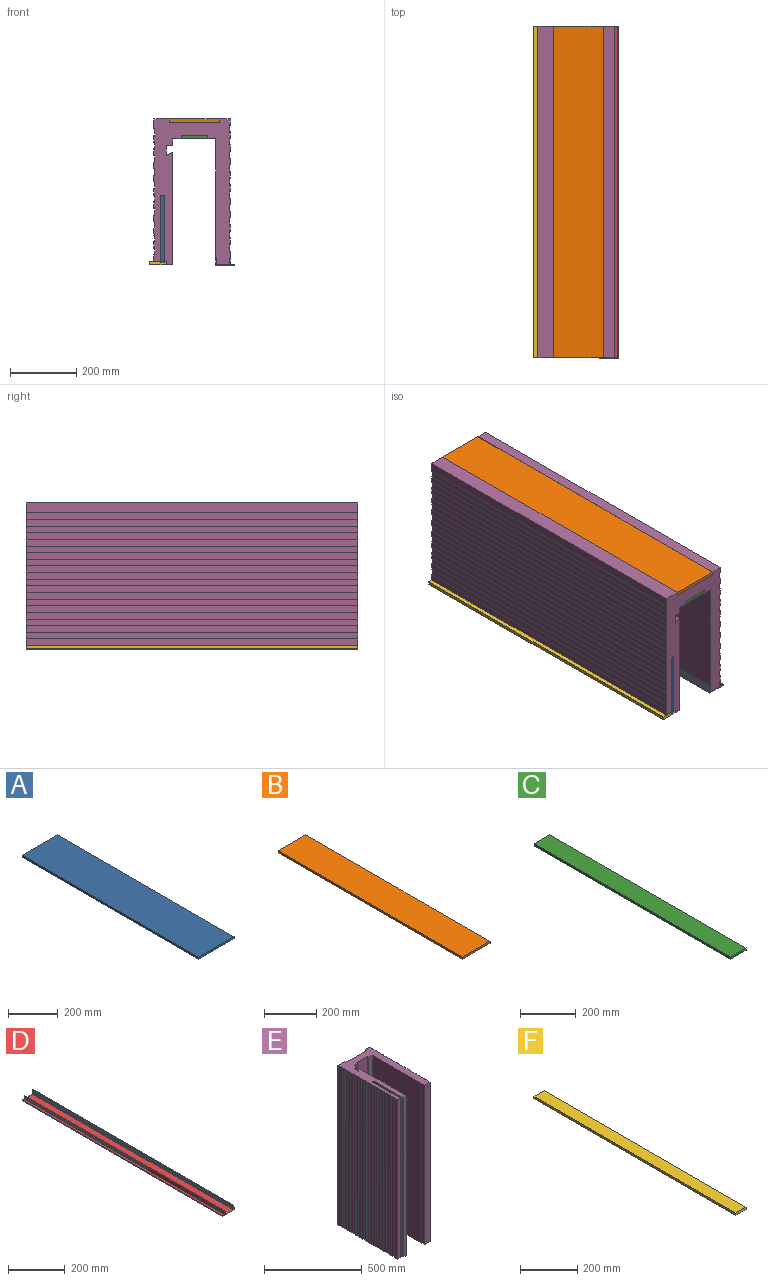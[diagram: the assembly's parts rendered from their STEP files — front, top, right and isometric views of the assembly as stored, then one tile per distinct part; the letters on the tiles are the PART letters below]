
ASSEMBLY  parts=6 mates=5
PART A: 6 faces, bbox 200x1000x10 mm
  f0: plane 1000x10mm, normal (-1,0,0), area 10000mm2, adj f1,f3,f4,f5
  f1: plane 1000x200mm, normal (0,0,-1), area 200000mm2, adj f0,f2,f4,f5
  f2: plane 1000x10mm, normal (1,0,0), area 10000mm2, adj f1,f3,f4,f5
  f3: plane 1000x200mm, normal (0,0,1), area 200000mm2, adj f0,f2,f4,f5
  f4: plane 200x10mm, normal (0,-1,0), area 2000mm2, adj f0,f1,f2,f3
  f5: plane 200x10mm, normal (0,1,0), area 2000mm2, adj f0,f1,f2,f3
PART B: 6 faces, bbox 150x1000x10 mm
  f0: plane 1000x10mm, normal (-1,0,0), area 10000mm2, adj f1,f3,f4,f5
  f1: plane 1000x150mm, normal (0,0,-1), area 150000mm2, adj f0,f2,f4,f5
  f2: plane 1000x10mm, normal (1,0,0), area 10000mm2, adj f1,f3,f4,f5
  f3: plane 1000x150mm, normal (0,0,1), area 150000mm2, adj f0,f2,f4,f5
  f4: plane 150x10mm, normal (0,-1,0), area 1500mm2, adj f0,f1,f2,f3
  f5: plane 150x10mm, normal (0,1,0), area 1500mm2, adj f0,f1,f2,f3
PART C: 6 faces, bbox 80x1000x10 mm
  f0: plane 1000x10mm, normal (-1,0,0), area 10000mm2, adj f1,f3,f4,f5
  f1: plane 1000x80mm, normal (0,0,-1), area 80000mm2, adj f0,f2,f4,f5
  f2: plane 1000x10mm, normal (1,0,0), area 10000mm2, adj f1,f3,f4,f5
  f3: plane 1000x80mm, normal (0,0,1), area 80000mm2, adj f0,f2,f4,f5
  f4: plane 80x10mm, normal (0,-1,0), area 800mm2, adj f0,f1,f2,f3
  f5: plane 80x10mm, normal (0,1,0), area 800mm2, adj f0,f1,f2,f3
PART D: 62 faces, bbox 57.5x1000x21 mm
  f0: plane 1000x14.3mm, normal (-1,0,0), area 14303.9mm2, adj f1,f2,f60,f61
  f1: plane 57.5x21mm, normal (0,-1,0), area 145.8mm2, adj f0,f2,f3,f4,f5,f6,f7,f8
  f2: plane 1000x11mm, normal (0,0,1), area 11000mm2, adj f0,f1,f3,f60
  f3: plane 1000x1.5mm, normal (1,0,0), area 1500mm2, adj f1,f2,f4,f60
  f4: plane 1000x1.5mm, normal (0,0,1), area 1500mm2, adj f1,f3,f5,f60
  f5: plane 1000x3mm, normal (-1,0,0), area 3000mm2, adj f1,f4,f6,f60
  f6: plane 1000x57.5mm, normal (0,0,-1), area 57500mm2, adj f1,f5,f7,f60
  f7: plane 1000x4mm, normal (1,0,0), area 4000mm2, adj f1,f6,f8,f60
  f8: plane 1000x1mm, normal (0,0,1), area 1000mm2, adj f1,f7,f9,f60
  f9: plane 1000x3mm, normal (-1,0,0), area 3000mm2, adj f1,f8,f10,f60
  f10: plane 1000x1mm, normal (0,0,1), area 1000mm2, adj f1,f9,f11,f60
  f11: plane 1000x7mm, normal (1,0,0), area 7000mm2, adj f1,f10,f12,f60
  f12: plane 1000x1mm, normal (0,0,-1), area 1000mm2, adj f1,f11,f13,f60
  f13: plane 1000x3mm, normal (-1,0,0), area 3000mm2, adj f1,f12,f14,f60
  f14: plane 1000x1mm, normal (0,0,-1), area 1000mm2, adj f1,f13,f15,f60
  f15: plane 1000x4mm, normal (1,0,0), area 4000mm2, adj f1,f14,f16,f60
  f16: plane 1000x2mm, normal (0,0,1), area 2000mm2, adj f1,f15,f17,f60
  f17: plane 1000x12mm, normal (1,0,0), area 12000mm2, adj f1,f16,f18,f60
  f18: plane 1000x1mm, normal (0,0,1), area 1000mm2, adj f1,f17,f19,f60
  f19: plane 1000x1.73mm, normal (-0.87,0,0.5), area 2000mm2, adj f1,f18,f20,f60
  f20: plane 1000x1mm, normal (0,0,-1), area 1000mm2, adj f1,f19,f21,f60
  f21: plane 1000x1.73mm, normal (-0.87,0,0.5), area 2000mm2, adj f1,f20,f22,f60
  f22: plane 1000x1mm, normal (0,0,-1), area 1000mm2, adj f1,f21,f23,f60
  f23: plane 1000x1.73mm, normal (-0.87,0,0.5), area 2000mm2, adj f1,f22,f24,f60
  f24: plane 1000x1mm, normal (0,0,-1), area 1000mm2, adj f1,f23,f25,f60
  f25: plane 1000x1.73mm, normal (-0.87,0,0.5), area 2000mm2, adj f1,f24,f26,f60
  f26: plane 1000x1mm, normal (0,0,-1), area 1000mm2, adj f1,f25,f27,f60
  f27: plane 1000x1.73mm, normal (-0.87,0,0.5), area 2000mm2, adj f1,f26,f28,f60
  f28: plane 1000x1mm, normal (0,0,-1), area 1000mm2, adj f1,f27,f29,f60
  f29: plane 1000x1.73mm, normal (-0.87,0,0.5), area 2000mm2, adj f1,f28,f30,f60
  f30: plane 1000x1mm, normal (0,0,-1), area 1000mm2, adj f1,f29,f31,f60
  f31: plane 1000x1.73mm, normal (-0.87,0,0.5), area 2000mm2, adj f1,f30,f32,f60
  f32: plane 1000x1mm, normal (0,0,-1), area 1000mm2, adj f1,f31,f33,f60
  f33: plane 1000x1.73mm, normal (-0.87,0,0.5), area 2000mm2, adj f1,f32,f34,f60
  f34: plane 1000x1mm, normal (0,0,-1), area 1000mm2, adj f1,f33,f35,f60
  f35: plane 1000x1.73mm, normal (-0.87,0,0.5), area 2000mm2, adj f1,f34,f36,f60
  f36: plane 1000x1mm, normal (0,0,-1), area 1000mm2, adj f1,f35,f37,f60
  f37: plane 1000x1.73mm, normal (-0.87,0,0.5), area 2000mm2, adj f1,f36,f38,f60
  f38: plane 1000x1mm, normal (0,0,-1), area 1000mm2, adj f1,f37,f39,f60
  f39: plane 1000x1.73mm, normal (-0.87,0,0.5), area 2000mm2, adj f1,f38,f40,f60
  f40: plane 1000x1mm, normal (0,0,-1), area 1000mm2, adj f1,f39,f41,f60
  f41: plane 1000x0.45mm, normal (-1,0,0), area 447.4mm2, adj f1,f40,f42,f60
  f42: plane 1000x41mm, normal (0,0,1), area 41000mm2, adj f1,f41,f43,f60
  f43: plane 1000x0.45mm, normal (1,0,0), area 447.4mm2, adj f1,f42,f44,f60
  f44: plane 1000x1mm, normal (0,0,-1), area 1000mm2, adj f1,f43,f45,f60
  f45: plane 1000x1.73mm, normal (0.87,0,0.5), area 2000mm2, adj f1,f44,f46,f60
  f46: plane 1000x1mm, normal (0,0,-1), area 1000mm2, adj f1,f45,f47,f60
  f47: plane 1000x1.73mm, normal (0.87,0,0.5), area 2000mm2, adj f1,f46,f48,f60
  f48: plane 1000x1mm, normal (0,0,-1), area 1000mm2, adj f1,f47,f49,f60
  f49: plane 1000x1.73mm, normal (0.87,0,0.5), area 2000mm2, adj f1,f48,f50,f60
  f50: plane 1000x1mm, normal (0,0,-1), area 1000mm2, adj f1,f49,f51,f60
  f51: plane 1000x1.73mm, normal (0.87,0,0.5), area 2000mm2, adj f1,f50,f52,f60
  f52: plane 1000x1mm, normal (0,0,-1), area 1000mm2, adj f1,f51,f53,f60
  f53: plane 1000x1.73mm, normal (0.87,0,0.5), area 2000mm2, adj f1,f52,f54,f60
  f54: plane 1000x1mm, normal (0,0,-1), area 1000mm2, adj f1,f53,f55,f60
  f55: plane 1000x1.73mm, normal (0.87,0,0.5), area 2000mm2, adj f1,f54,f56,f60
  f56: plane 1000x1mm, normal (0,0,-1), area 1000mm2, adj f1,f55,f57,f60
  f57: plane 1000x1.73mm, normal (0.87,0,0.5), area 2000mm2, adj f1,f56,f58,f60
  f58: plane 1000x1mm, normal (0,0,-1), area 1000mm2, adj f1,f57,f59,f60
  f59: plane 1000x1.73mm, normal (0.87,0,0.5), area 2000mm2, adj f1,f58,f60,f61
  f60: plane 57.5x21mm, normal (0,1,0), area 145.8mm2, adj f0,f2,f3,f4,f5,f6,f7,f8
  f61: plane 1000x1mm, normal (0,0,1), area 1000mm2, adj f0,f1,f59,f60
PART E: 112 faces, bbox 230x440x1000 mm
  f0: plane 1000x20mm, normal (-1,0,0), area 20000mm2, adj f50,f51,f106,f110
  f1: plane 1000x20mm, normal (-1,0,0), area 20000mm2, adj f50,f51,f103,f107
  f2: plane 1000x20mm, normal (-1,0,0), area 20000mm2, adj f50,f51,f100,f104
  f3: plane 1000x20mm, normal (-1,0,0), area 20000mm2, adj f50,f51,f97,f101
  f4: plane 1000x20mm, normal (-1,0,0), area 20000mm2, adj f50,f51,f94,f98
  f5: plane 1000x20mm, normal (-1,0,0), area 20000mm2, adj f50,f51,f91,f95
  f6: plane 1000x20mm, normal (-1,0,0), area 20000mm2, adj f50,f51,f88,f92
  f7: plane 1000x20mm, normal (-1,0,0), area 20000mm2, adj f50,f51,f85,f89
  f8: plane 1000x20mm, normal (-1,0,0), area 20000mm2, adj f50,f51,f82,f86
  f9: plane 1000x30mm, normal (-1,0,0), area 30000mm2, adj f21,f50,f51,f83
  f10: plane 1000x22mm, normal (1,0,0), area 22000mm2, adj f45,f50,f51,f79
  f11: plane 1000x20mm, normal (1,0,0), area 20000mm2, adj f50,f51,f76,f80
  f12: plane 1000x20mm, normal (1,0,0), area 20000mm2, adj f50,f51,f73,f77
  f13: plane 1000x20mm, normal (1,0,0), area 20000mm2, adj f50,f51,f70,f74
  f14: plane 1000x20mm, normal (1,0,0), area 20000mm2, adj f50,f51,f67,f71
  f15: plane 1000x20mm, normal (1,0,0), area 20000mm2, adj f50,f51,f64,f68
  f16: plane 1000x20mm, normal (1,0,0), area 20000mm2, adj f50,f51,f61,f65
  f17: plane 1000x20mm, normal (1,0,0), area 20000mm2, adj f50,f51,f58,f62
  f18: plane 1000x20mm, normal (1,0,0), area 20000mm2, adj f50,f51,f55,f59
  f19: plane 1000x20mm, normal (1,0,0), area 20000mm2, adj f50,f51,f52,f56
  f20: plane 1000x10mm, normal (1,0,0), area 10000mm2, adj f21,f49,f50,f51
  f21: plane 1000x46.75mm, normal (0,1,0), area 46750mm2, adj f9,f20,f50,f51
  f22: plane 1000x20mm, normal (-1,0,0), area 20000mm2, adj f23,f50,f51,f109
  f23: plane 1000x20.5mm, normal (0,-1,0), area 20500mm2, adj f22,f24,f50,f51
  f24: plane 1000x200mm, normal (1,0,0), area 200000mm2, adj f23,f25,f50,f51
  f25: cylinder r=10mm len=1000mm, axis (0,0,-1), area 11054.3mm2, adj f24,f26,f50,f51
  f26: plane 1000x200mm, normal (-1,0,0), area 200000mm2, adj f25,f27,f50,f51
  f27: plane 1000x6mm, normal (0,-1,0), area 6000mm2, adj f26,f28,f50,f51
  f28: plane 1000x10mm, normal (-1,0,0), area 10000mm2, adj f27,f29,f50,f51
  f29: plane 1000x20mm, normal (0,-1,0), area 20000mm2, adj f28,f30,f50,f51
  f30: plane 1000x340.19mm, normal (1,0,0), area 340190.5mm2, adj f29,f31,f50,f51
  f31: plane 1000x20mm, normal (-0.45,0.89,0), area 22446.5mm2, adj f30,f32,f50,f51
  f32: plane 1000x30mm, normal (1,0,0), area 30000mm2, adj f31,f33,f50,f51
  f33: plane 1000x20mm, normal (0,-1,0), area 20000mm2, adj f32,f34,f50,f51
  f34: plane 1000x20mm, normal (1,0,0), area 20000mm2, adj f33,f35,f50,f51
  f35: plane 1000x24.75mm, normal (0,-1,0), area 24750mm2, adj f34,f36,f50,f51
  f36: plane 1000x10mm, normal (1,0,0), area 10000mm2, adj f35,f37,f50,f51
  f37: plane 1000x80.5mm, normal (0,-1,0), area 80500mm2, adj f36,f38,f50,f51
  f38: plane 1000x10mm, normal (-1,0,0), area 10000mm2, adj f37,f39,f50,f51
  f39: plane 1000x24.75mm, normal (0,-1,0), area 24750mm2, adj f38,f40,f50,f51
  f40: plane 1000x357.5mm, normal (-1,0,0), area 357500mm2, adj f39,f41,f50,f51
  f41: plane 1000x2mm, normal (0,-1,0), area 2000mm2, adj f40,f42,f50,f51
  f42: plane 1000x21.5mm, normal (-1,0,0), area 21500mm2, adj f41,f43,f50,f51
  f43: plane 1000x39.1mm, normal (0,-1,0), area 39100mm2, adj f42,f44,f50,f51
  f44: plane 1000x18.5mm, normal (1,0,0), area 18500mm2, adj f43,f45,f50,f51
  f45: plane 1000x1.9mm, normal (0,-1,0), area 1900mm2, adj f10,f44,f50,f51
  f46: plane 1000x18.5mm, normal (1,0,0), area 18500mm2, adj f47,f50,f51,f53
  f47: plane 1000x32.75mm, normal (0,1,0), area 32750mm2, adj f46,f48,f50,f51
  f48: plane 1000x10mm, normal (-1,0,0), area 10000mm2, adj f47,f49,f50,f51
  f49: plane 1000x150.5mm, normal (0,1,0), area 150500mm2, adj f20,f48,f50,f51
  f50: plane 440x230mm, normal (0,0,1), area 45531.3mm2, adj f0,f1,f2,f3,f4,f5,f6,f7
  f51: plane 440x230mm, normal (0,0,-1), area 45531.3mm2, adj f0,f1,f2,f3,f4,f5,f6,f7
  f52: plane 1000x2mm, normal (-0.71,0.71,0), area 2828.4mm2, adj f19,f50,f51,f54
  f53: plane 1000x2mm, normal (-0.71,-0.71,0), area 2828.4mm2, adj f46,f50,f51,f54
  f54: plane 1000x24mm, normal (1,0,0), area 24000mm2, adj f50,f51,f52,f53
  f55: plane 1000x2mm, normal (-0.71,0.71,0), area 2828.4mm2, adj f18,f50,f51,f57
  f56: plane 1000x2mm, normal (-0.71,-0.71,0), area 2828.4mm2, adj f19,f50,f51,f57
  f57: plane 1000x24mm, normal (1,0,0), area 24000mm2, adj f50,f51,f55,f56
  f58: plane 1000x2mm, normal (-0.71,0.71,0), area 2828.4mm2, adj f17,f50,f51,f60
  f59: plane 1000x2mm, normal (-0.71,-0.71,0), area 2828.4mm2, adj f18,f50,f51,f60
  f60: plane 1000x24mm, normal (1,0,0), area 24000mm2, adj f50,f51,f58,f59
  f61: plane 1000x2mm, normal (-0.71,0.71,0), area 2828.4mm2, adj f16,f50,f51,f63
  f62: plane 1000x2mm, normal (-0.71,-0.71,0), area 2828.4mm2, adj f17,f50,f51,f63
  f63: plane 1000x24mm, normal (1,0,0), area 24000mm2, adj f50,f51,f61,f62
  f64: plane 1000x2mm, normal (-0.71,0.71,0), area 2828.4mm2, adj f15,f50,f51,f66
  f65: plane 1000x2mm, normal (-0.71,-0.71,0), area 2828.4mm2, adj f16,f50,f51,f66
  f66: plane 1000x24mm, normal (1,0,0), area 24000mm2, adj f50,f51,f64,f65
  f67: plane 1000x2mm, normal (-0.71,0.71,0), area 2828.4mm2, adj f14,f50,f51,f69
  f68: plane 1000x2mm, normal (-0.71,-0.71,0), area 2828.4mm2, adj f15,f50,f51,f69
  f69: plane 1000x24mm, normal (1,0,0), area 24000mm2, adj f50,f51,f67,f68
  f70: plane 1000x2mm, normal (-0.71,0.71,0), area 2828.4mm2, adj f13,f50,f51,f72
  f71: plane 1000x2mm, normal (-0.71,-0.71,0), area 2828.4mm2, adj f14,f50,f51,f72
  f72: plane 1000x24mm, normal (1,0,0), area 24000mm2, adj f50,f51,f70,f71
  f73: plane 1000x2mm, normal (-0.71,0.71,0), area 2828.4mm2, adj f12,f50,f51,f75
  f74: plane 1000x2mm, normal (-0.71,-0.71,0), area 2828.4mm2, adj f13,f50,f51,f75
  f75: plane 1000x24mm, normal (1,0,0), area 24000mm2, adj f50,f51,f73,f74
  f76: plane 1000x2mm, normal (-0.71,0.71,0), area 2828.4mm2, adj f11,f50,f51,f78
  f77: plane 1000x2mm, normal (-0.71,-0.71,0), area 2828.4mm2, adj f12,f50,f51,f78
  f78: plane 1000x24mm, normal (1,0,0), area 24000mm2, adj f50,f51,f76,f77
  f79: plane 1000x2mm, normal (-0.71,0.71,0), area 2828.4mm2, adj f10,f50,f51,f81
  f80: plane 1000x2mm, normal (-0.71,-0.71,0), area 2828.4mm2, adj f11,f50,f51,f81
  f81: plane 1000x24mm, normal (1,0,0), area 24000mm2, adj f50,f51,f79,f80
  f82: plane 1000x2mm, normal (0.71,0.71,0), area 2828.4mm2, adj f8,f50,f51,f84
  f83: plane 1000x2mm, normal (0.71,-0.71,0), area 2828.4mm2, adj f9,f50,f51,f84
  f84: plane 1000x24mm, normal (-1,0,0), area 24000mm2, adj f50,f51,f82,f83
  f85: plane 1000x2mm, normal (0.71,0.71,0), area 2828.4mm2, adj f7,f50,f51,f87
  f86: plane 1000x2mm, normal (0.71,-0.71,0), area 2828.4mm2, adj f8,f50,f51,f87
  f87: plane 1000x24mm, normal (-1,0,0), area 24000mm2, adj f50,f51,f85,f86
  f88: plane 1000x2mm, normal (0.71,0.71,0), area 2828.4mm2, adj f6,f50,f51,f90
  f89: plane 1000x2mm, normal (0.71,-0.71,0), area 2828.4mm2, adj f7,f50,f51,f90
  f90: plane 1000x24mm, normal (-1,0,0), area 24000mm2, adj f50,f51,f88,f89
  f91: plane 1000x2mm, normal (0.71,0.71,0), area 2828.4mm2, adj f5,f50,f51,f93
  f92: plane 1000x2mm, normal (0.71,-0.71,0), area 2828.4mm2, adj f6,f50,f51,f93
  f93: plane 1000x24mm, normal (-1,0,0), area 24000mm2, adj f50,f51,f91,f92
  f94: plane 1000x2mm, normal (0.71,0.71,0), area 2828.4mm2, adj f4,f50,f51,f96
  f95: plane 1000x2mm, normal (0.71,-0.71,0), area 2828.4mm2, adj f5,f50,f51,f96
  f96: plane 1000x24mm, normal (-1,0,0), area 24000mm2, adj f50,f51,f94,f95
  f97: plane 1000x2mm, normal (0.71,0.71,0), area 2828.4mm2, adj f3,f50,f51,f99
  f98: plane 1000x2mm, normal (0.71,-0.71,0), area 2828.4mm2, adj f4,f50,f51,f99
  f99: plane 1000x24mm, normal (-1,0,0), area 24000mm2, adj f50,f51,f97,f98
  f100: plane 1000x2mm, normal (0.71,0.71,0), area 2828.4mm2, adj f2,f50,f51,f102
  f101: plane 1000x2mm, normal (0.71,-0.71,0), area 2828.4mm2, adj f3,f50,f51,f102
  f102: plane 1000x24mm, normal (-1,0,0), area 24000mm2, adj f50,f51,f100,f101
  f103: plane 1000x2mm, normal (0.71,0.71,0), area 2828.4mm2, adj f1,f50,f51,f105
  f104: plane 1000x2mm, normal (0.71,-0.71,0), area 2828.4mm2, adj f2,f50,f51,f105
  f105: plane 1000x24mm, normal (-1,0,0), area 24000mm2, adj f50,f51,f103,f104
  f106: plane 1000x2mm, normal (0.71,0.71,0), area 2828.4mm2, adj f0,f50,f51,f108
  f107: plane 1000x2mm, normal (0.71,-0.71,0), area 2828.4mm2, adj f1,f50,f51,f108
  f108: plane 1000x24mm, normal (-1,0,0), area 24000mm2, adj f50,f51,f106,f107
  f109: plane 1000x2mm, normal (0.71,0.71,0), area 2828.4mm2, adj f22,f50,f51,f111
  f110: plane 1000x2mm, normal (0.71,-0.71,0), area 2828.4mm2, adj f0,f50,f51,f111
  f111: plane 1000x24mm, normal (-1,0,0), area 24000mm2, adj f50,f51,f109,f110
PART F: 6 faces, bbox 50x1000x10 mm
  f0: plane 1000x10mm, normal (-1,0,0), area 10000mm2, adj f1,f3,f4,f5
  f1: plane 1000x50mm, normal (0,0,-1), area 50000mm2, adj f0,f2,f4,f5
  f2: plane 1000x10mm, normal (1,0,0), area 10000mm2, adj f1,f3,f4,f5
  f3: plane 1000x50mm, normal (0,0,1), area 50000mm2, adj f0,f2,f4,f5
  f4: plane 50x10mm, normal (0,-1,0), area 500mm2, adj f0,f1,f2,f3
  f5: plane 50x10mm, normal (0,1,0), area 500mm2, adj f0,f1,f2,f3
PLACE A rot(axis=(0,1,0),90deg) t=(-216.83,500,-166.72)mm
PLACE B t=(-190.83,500,55.28)mm fixed
PLACE C t=(-155.83,500,5.28)mm
PLACE D rot(axis=(0,0,1),180deg) t=(-52.58,-500,-375.22)mm
PLACE E rot(axis=(1,0,0),90deg) t=(-169.34,500,-104.89)mm
PLACE F t=(-250.58,500,-374.72)mm
MATE fastened A.f4 <-> E.f50  axis (0,-1,0) through (-206.58,-500,-164.72)mm
MATE fastened E.f50 <-> B.f4  axis (0,-1,0) through (-190.83,-500,65.28)mm
MATE fastened C.f4 <-> E.f50  axis (0,-1,0) through (-155.83,-500,15.28)mm
MATE fastened D.f60 <-> E.f50  axis (0,-1,0) through (-48.58,-500,-373.72)mm
MATE fastened F.f4 <-> E.f50  axis (0,-1,0) through (-200.58,-500,-364.72)mm
